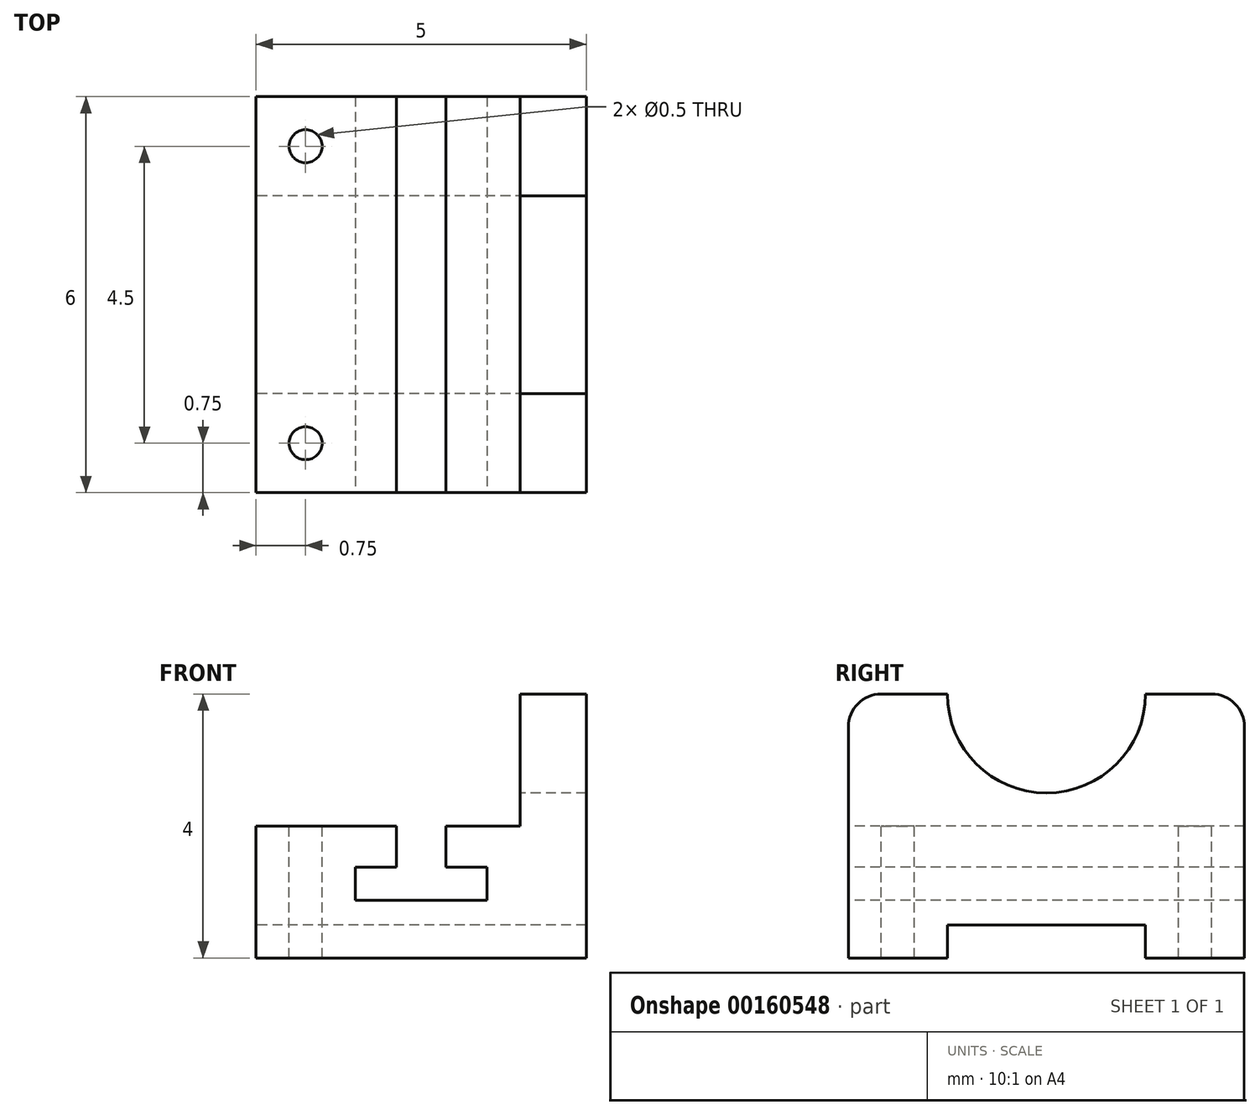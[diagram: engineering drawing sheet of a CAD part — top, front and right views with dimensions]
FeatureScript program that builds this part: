
annotation { "Feature Type Name" : "Feature", "Feature Type Description" : "" }
export const myFeature = defineFeature(function(context is Context, id is Id, definition is map)
    precondition{}
    {
        {
            var Q0;
            Q0=qCreatedBy(makeId("Front.planeOp"),FACE);
            var sketch = newSketch(context, id + "F0", { "sketchPlane" : qUnion([Q0])});
            skLineSegment(sketch, "E0", {"start": v(0, 0) * mm, "end": v(5, 0) * mm});
            skLineSegment(sketch, "E1", {"start": v(0, 0) * mm, "end": v(0, 2) * mm});
            skLineSegment(sketch, "E2", {"start": v(0, 2) * mm, "end": v(4, 2) * mm});
            skLineSegment(sketch, "E3", {"start": v(5, 0) * mm, "end": v(5, 4) * mm});
            skLineSegment(sketch, "E4", {"start": v(5, 4) * mm, "end": v(4, 4) * mm});
            skLineSegment(sketch, "E5", {"start": v(4, 2) * mm, "end": v(4, 4) * mm});
            skSolve(sketch);
        }
        {
            var Q0;
            Q0 = qSketchRegion(id + "F0", true);
            extrude(context, id + "F1", {"entities" : qUnion([Q0]), "oppositeDirection" : true, "depth" : 6 * mm});
        }
        {
            var Q0;
            Q0=makeQuery(id+"F1.opExtrude","CAP_FACE",FACE,{"disambiguationData":[OSD([sQuery(id+"F0.wireOp",EDGE,"E0"),sQuery(id+"F0.wireOp",EDGE,"E1"),sQuery(id+"F0.wireOp",EDGE,"E2"),sQuery(id+"F0.wireOp",EDGE,"E3"),sQuery(id+"F0.wireOp",EDGE,"E4"),sQuery(id+"F0.wireOp",EDGE,"E5")])],"isStart":true});
            var sketch = newSketch(context, id + "F2", { "sketchPlane" : qUnion([Q0])});
            skLineSegment(sketch, "E6", {"start": v(0, 2) * mm, "end": v(2.12, 2) * mm, "construction": true});
            skLineSegment(sketch, "E7", {"start": v(2.12, 2) * mm, "end": v(2.12, 1.38) * mm});
            skLineSegment(sketch, "E8", {"start": v(2.12, 2) * mm, "end": v(2.88, 2) * mm});
            skLineSegment(sketch, "E9", {"start": v(2.88, 2) * mm, "end": v(2.88, 1.38) * mm});
            skPoint(sketch, "E10", {"position": v(2.5, 2) * mm});
            skLineSegment(sketch, "E11", {"start": v(2.5, 2) * mm, "end": v(2.5, 0.87) * mm, "construction": true});
            skLineSegment(sketch, "E12", {"start": v(1.5, 0.87) * mm, "end": v(3.5, 0.87) * mm});
            skLineSegment(sketch, "E13", {"start": v(2.12, 1.38) * mm, "end": v(1.5, 1.38) * mm});
            skLineSegment(sketch, "E14", {"start": v(1.5, 1.37) * mm, "end": v(1.5, 0.88) * mm});
            skLineSegment(sketch, "E15", {"start": v(2.88, 1.38) * mm, "end": v(3.5, 1.38) * mm});
            skLineSegment(sketch, "E16", {"start": v(3.5, 1.38) * mm, "end": v(3.5, 0.87) * mm});
            skSolve(sketch);
        }
        {
            var Q0;
            Q0 = qSketchRegion(id + "F2", true);
            extrude(context, id + "F3", {"entities" : qUnion([Q0]), "operationType" : NewBodyOperationType.REMOVE, "oppositeDirection" : true, "depth" : 25 * mm});
        }
        {
            var Q0;
            Q0=makeQuery(id+"F1.opExtrude","SWEPT_FACE",FACE,{"disambiguationData":[OSD([sQuery(id+"F0.wireOp",EDGE,"E1")])]});
            var sketch = newSketch(context, id + "F4", { "sketchPlane" : qUnion([Q0])});
            skLineSegment(sketch, "E17", {"start": v(-4.5, 0) * mm, "end": v(-1.5, 0) * mm});
            skLineSegment(sketch, "E18", {"start": v(-4.5, 0) * mm, "end": v(-4.5, 0.5) * mm});
            skLineSegment(sketch, "E19", {"start": v(-4.5, 0.5) * mm, "end": v(-1.5, 0.5) * mm});
            skLineSegment(sketch, "E20", {"start": v(-1.5, 0.5) * mm, "end": v(-1.5, 0) * mm});
            skSolve(sketch);
        }
        {
            var Q0;
            Q0 = qSketchRegion(id + "F4", true);
            extrude(context, id + "F5", {"entities" : qUnion([Q0]), "operationType" : NewBodyOperationType.REMOVE, "oppositeDirection" : true, "depth" : 25 * mm});
        }
        {
            var Q0;
            {var subQ3=sQuery(id+"F0.wireOp",EDGE,"E2");var subQ4=sQuery(id+"F0.wireOp",EDGE,"E1");Q0=makeQuery(id+"F3.boolean.opBoolean","SPLIT",FACE,{"disambiguationData":[TD([makeQuery(id+"F1.opExtrude","SWEPT_FACE",FACE,{"disambiguationData":[OSD([subQ4])]})])],"derivedFrom":makeQuery(id+"F1.opExtrude","SWEPT_FACE",FACE,{"disambiguationData":[OSD([subQ3])]})});}
            var sketch = newSketch(context, id + "F6", { "sketchPlane" : qUnion([Q0])});
            skCircle(sketch, "E21", {"center": v(0.75, 0.75) * mm, "radius": 0.25 * mm});
            skCircle(sketch, "E22", {"center": v(0.75, 5.25) * mm, "radius": 0.25 * mm});
            skSolve(sketch);
        }
        {
            var Q0;
            Q0 = qSketchRegion(id + "F6", true);
            extrude(context, id + "F7", {"entities" : qUnion([Q0]), "operationType" : NewBodyOperationType.REMOVE, "oppositeDirection" : true, "depth" : 25 * mm});
        }
        {
            var Q0;
            Q0=makeQuery(id+"F1.opExtrude","SWEPT_FACE",FACE,{"disambiguationData":[OSD([sQuery(id+"F0.wireOp",EDGE,"E5")])]});
            var sketch = newSketch(context, id + "F8", { "sketchPlane" : qUnion([Q0])});
            skArc(sketch, "E23", {"start": v(-4.5, 4) * mm, "mid": v(-3, 2.5) * mm, "end": v(-1.5, 4) * mm});
            skLineSegment(sketch, "E24", {"start": v(-4.5, 4) * mm, "end": v(-1.5, 4) * mm});
            skSolve(sketch);
        }
        {
            var Q0;
            Q0 = qSketchRegion(id + "F8", true);
            extrude(context, id + "F9", {"entities" : qUnion([Q0]), "operationType" : NewBodyOperationType.REMOVE, "oppositeDirection" : true, "depth" : 25 * mm});
        }
        {
            var Q0;
            Q0=makeQuery(id+"F1.opExtrude","CAP_EDGE",EDGE,{"disambiguationData":[OSD([sQuery(id+"F0.wireOp",EDGE,"E4")])],"isStart":true});
            var Q1;
            Q1=makeQuery(id+"F1.opExtrude","CAP_EDGE",EDGE,{"disambiguationData":[OSD([sQuery(id+"F0.wireOp",EDGE,"E4")])],"isStart":false});
            fillet(context, id + "F10", {"entities" : qUnion([Q0, Q1]), "radius" : 0.5 * mm, "tangentPropagation" : true, "allowEdgeOverflow" : false});
        }
    });
